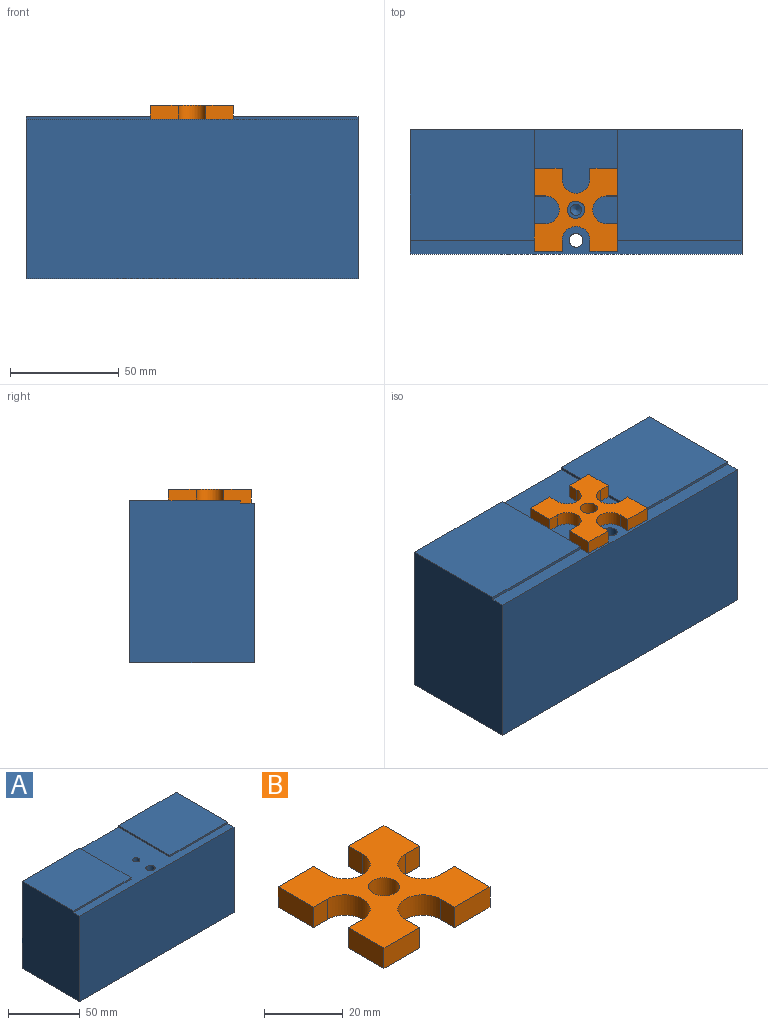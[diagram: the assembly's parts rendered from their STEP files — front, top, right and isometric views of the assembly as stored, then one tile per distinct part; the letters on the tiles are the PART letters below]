
ASSEMBLY  parts=2 mates=1
PART A: 15 faces, bbox 152.4x57.2x74.4 mm
  f0: plane 57.02x1.27mm, normal (0,-1,0), area 72.4mm2, adj f4,f7,f9,f12
  f1: plane 57.02x50.8mm, normal (0,0,1), area 2896.8mm2, adj f2,f3,f6,f11
  f2: plane 152.4x74.37mm, normal (0,1,0), area 11285.5mm2, adj f1,f4,f6,f7,f8,f9,f11,f12
  f3: plane 57.02x1.27mm, normal (0,-1,0), area 72.4mm2, adj f1,f6,f9,f11
  f4: plane 57.02x50.8mm, normal (0,0,1), area 2896.8mm2, adj f0,f2,f7,f12
  f5: plane 152.4x73.1mm, normal (0,-1,0), area 11140.6mm2, adj f6,f7,f8,f9
  f6: plane 74.37x57.15mm, normal (1,0,0), area 4242.2mm2, adj f1,f2,f3,f5,f8,f9
  f7: plane 74.37x57.15mm, normal (-1,0,0), area 4242.2mm2, adj f0,f2,f4,f5,f8,f9
  f8: plane 152.4x57.15mm, normal (0,0,-1), area 8678mm2, adj f2,f5,f6,f7,f10
  f9: plane 152.4x57.15mm, normal (0,0,1), area 2864mm2, adj f0,f2,f3,f5,f6,f7,f10,f11
  f10: cylinder r=3.17mm len=73.1mm, axis (0,0,1), area 1458.3mm2, adj f8,f9
  f11: plane 50.8x1.27mm, normal (-1,0,0), area 64.5mm2, adj f1,f2,f3,f9
  f12: plane 50.8x1.27mm, normal (1,0,0), area 64.5mm2, adj f0,f2,f4,f9
  f13: cone r=0mm half-angle=59deg, axis (0,0,1), area 23.9mm2, adj f14
  f14: cylinder r=2.55mm len=12.7mm, axis (0,0,1), area 203.7mm2, adj f9,f13
PART B: 23 faces, bbox 38.1x38.1x6.4 mm
  f0: plane 6.35x5.08mm, normal (-1,0,0), area 32.2mm2, adj f1,f20,f21,f22
  f1: cylinder r=6.35mm len=12.7mm, axis (0,0,-1), area 126.7mm2, adj f0,f2,f21,f22
  f2: plane 6.35x5.08mm, normal (1,0,0), area 32.2mm2, adj f1,f3,f21,f22
  f3: plane 12.7x6.35mm, normal (0,1,0), area 80.7mm2, adj f2,f4,f21,f22
  f4: plane 12.7x6.35mm, normal (-1,0,0), area 80.6mm2, adj f3,f5,f21,f22
  f5: plane 6.35x5.08mm, normal (0,-1,0), area 32.2mm2, adj f4,f6,f21,f22
  f6: cylinder r=6.35mm len=12.7mm, axis (0,0,-1), area 126.7mm2, adj f5,f7,f21,f22
  f7: plane 6.35x5.08mm, normal (0,1,0), area 32.2mm2, adj f6,f8,f21,f22
  f8: plane 12.7x6.35mm, normal (-1,0,0), area 80.6mm2, adj f7,f9,f21,f22
  f9: plane 12.7x6.35mm, normal (0,-1,0), area 80.7mm2, adj f8,f10,f21,f22
  f10: plane 6.35x5.08mm, normal (1,0,0), area 32.2mm2, adj f9,f11,f21,f22
  f11: cylinder r=6.35mm len=12.7mm, axis (0,0,-1), area 126.7mm2, adj f10,f12,f21,f22
  f12: plane 6.35x5.08mm, normal (-1,0,0), area 32.2mm2, adj f11,f13,f21,f22
  f13: plane 12.7x6.35mm, normal (0,-1,0), area 80.6mm2, adj f12,f14,f21,f22
  f14: plane 12.7x6.35mm, normal (1,0,0), area 80.6mm2, adj f13,f15,f21,f22
  f15: plane 6.35x5.08mm, normal (0,1,0), area 32.2mm2, adj f14,f16,f21,f22
  f16: cylinder r=6.35mm len=12.7mm, axis (0,0,-1), area 126.7mm2, adj f15,f17,f21,f22
  f17: plane 6.35x5.08mm, normal (0,-1,0), area 32.2mm2, adj f16,f18,f21,f22
  f18: plane 12.7x6.35mm, normal (1,0,0), area 80.7mm2, adj f17,f20,f21,f22
  f19: cylinder r=3.98mm len=7.95mm, axis (0,0,-1), area 158.6mm2, adj f21,f22
  f20: plane 12.7x6.35mm, normal (0,1,0), area 80.6mm2, adj f0,f18,f21,f22
  f21: plane 38.1x38.1mm, normal (0,0,1), area 890.6mm2, adj f0,f1,f2,f3,f4,f5,f6,f7
  f22: plane 38.1x38.1mm, normal (0,0,-1), area 890.6mm2, adj f0,f1,f2,f3,f4,f5,f6,f7
PLACE A t=(1.42,10.48,3.22)mm
PLACE B t=(-93.83,11.75,1.95)mm
MATE fastened B.f19 <-> A.f13  axis (0,0,-1) through (-74.78,30.8,1.95)mm
